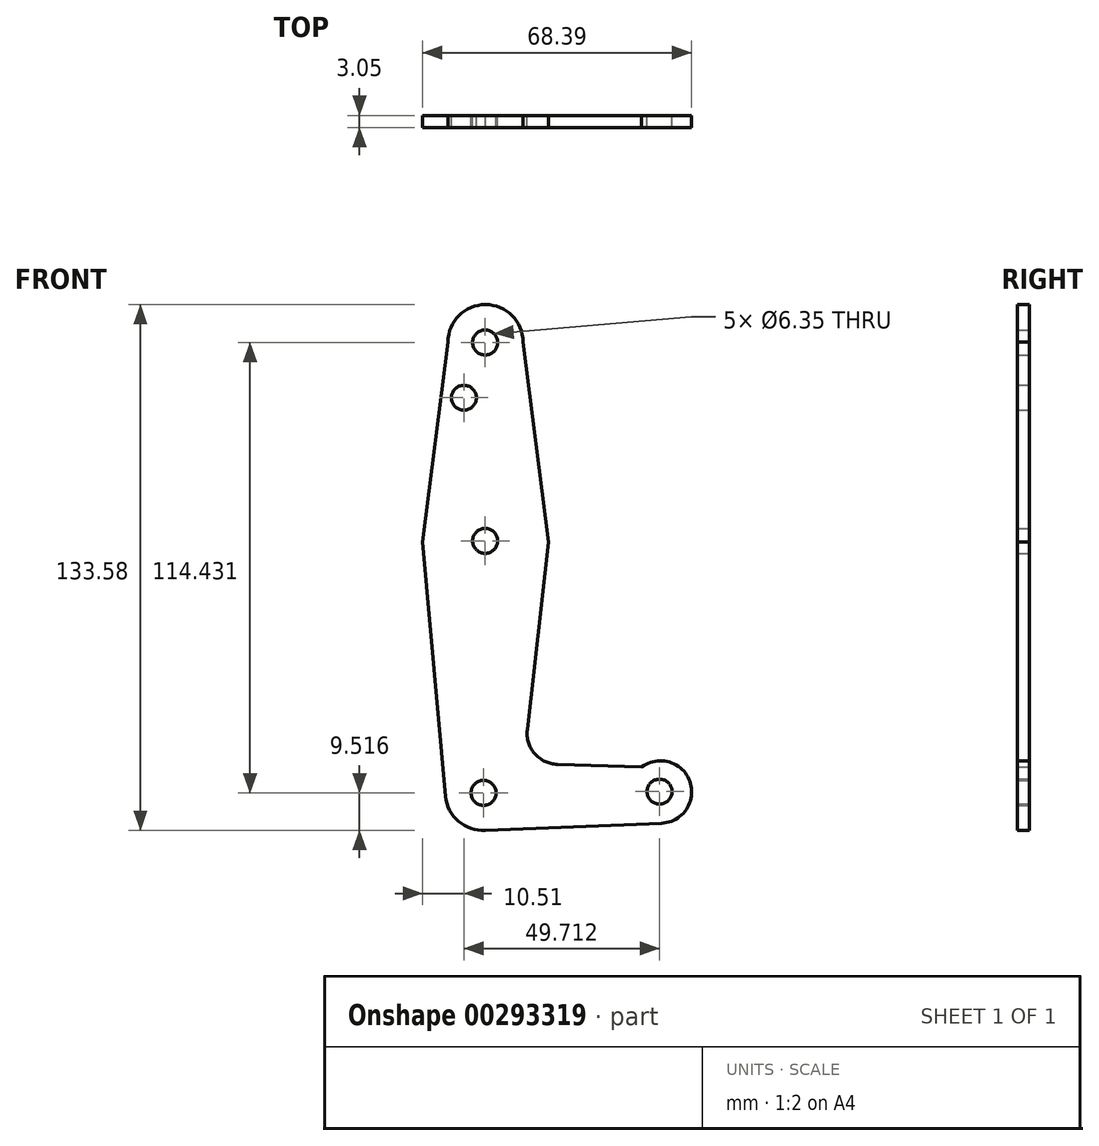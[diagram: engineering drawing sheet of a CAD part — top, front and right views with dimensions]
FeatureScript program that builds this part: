
annotation { "Feature Type Name" : "Feature", "Feature Type Description" : "" }
export const myFeature = defineFeature(function(context is Context, id is Id, definition is map)
    precondition{}
    {
        {
            var Q0;
            Q0=qCreatedBy(makeId("Front.planeOp"),FACE);
            var sketch = newSketch(context, id + "F0", { "sketchPlane" : qUnion([Q0])});
            skLineSegment(sketch, "E0", {"start": v(0, 0) * mm, "end": v(0, 50.8) * mm});
            skLineSegment(sketch, "E1", {"start": v(0, 0) * mm, "end": v(0, -63.5) * mm});
            skCircle(sketch, "E2", {"center": v(0, 50.8) * mm, "radius": 9.53 * mm});
            skCircle(sketch, "E3", {"center": v(0, 0) * mm, "radius": 15.88 * mm});
            skLineSegment(sketch, "E4", {"start": v(0, -63.5) * mm, "end": v(44.45, -63.5) * mm});
            skCircle(sketch, "E5", {"center": v(44.45, -63.5) * mm, "radius": 7.94 * mm});
            skCircle(sketch, "E6", {"center": v(-0.7, -63.72) * mm, "radius": 9.53 * mm});
            skLineSegment(sketch, "E7", {"start": v(-9.52, 50.84) * mm, "end": v(-16, 0) * mm});
            skLineSegment(sketch, "E8", {"start": v(9.53, 50.8) * mm, "end": v(16, 0) * mm});
            skLineSegment(sketch, "E9", {"start": v(-16, 0) * mm, "end": v(-10.18, -64.58) * mm});
            skLineSegment(sketch, "E10", {"start": v(10.62, -47.67) * mm, "end": v(16, 0) * mm});
            skLineSegment(sketch, "E11", {"start": v(18.28, -56.5) * mm, "end": v(46.23, -57.35) * mm});
            skLineSegment(sketch, "E12", {"start": v(0, -73.22) * mm, "end": v(44.77, -71.43) * mm});
            skCircle(sketch, "E13", {"center": v(-5.5, 36.66) * mm, "radius": 3.18 * mm});
            skCircle(sketch, "E14", {"center": v(-0.09, 50.7) * mm, "radius": 3.18 * mm});
            skCircle(sketch, "E15", {"center": v(-0.09, 0.3) * mm, "radius": 3.18 * mm});
            skCircle(sketch, "E16", {"center": v(-0.5, -63.73) * mm, "radius": 3.18 * mm});
            skCircle(sketch, "E17", {"center": v(44.22, -63.42) * mm, "radius": 3.18 * mm});
            skArc(sketch, "E18.filletArc", {"start": v(10.62, -47.67) * mm, "mid": v(12.5, -53.77) * mm, "end": v(18.28, -56.5) * mm});
            skSolve(sketch);
        }
        {
            var Q0;
            Q0 = qSketchRegion(id + "F0", true);
            var Q1;
            {var subQ0=sQuery(id+"F0.wireOp",EDGE,"E6");var subQ1=sQuery(id+"F0.wireOp",EDGE,"E1");var subQ2=makeQuery(id+"F0.imprint","INTERSECT",VERTEX,{"derivedFrom":[subQ1,subQ0]});Q1=makeQuery(id+"F0.imprint","IMPRINT",FACE,{"disambiguationData":[TD([[makeQuery(id+"F0.imprint","IMPRINT",EDGE,{"disambiguationData":[TD([[subQ2,-1.0]])],"derivedFrom":subQ1}),1.0]])]});}
            extrude(context, id + "F1", {"entities" : qUnion([Q0, Q1]), "depth" : 3.05 * mm});
        }
    });
